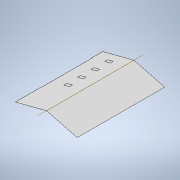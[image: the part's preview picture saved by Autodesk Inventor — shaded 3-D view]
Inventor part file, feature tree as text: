
AUTODESK INVENTOR PART (.ipt)
format: ipt  version: 2022.1 (Build 261234000, 234)  size: 143,872 bytes
history: native  units: in
note: dims shown in document units (in); Inventor stores cm internally (conversion verified against a paired STEP export)
features: other x2, sketch x2, extrude x2
ambient origin geometry x8: Origin, YZ Plane, XZ Plane, XY Plane, X Axis, Y Axis, Z Axis, Center Point
bodies: Body1 (feature_tree)
feature tree (6):
  other  "southPlaneOfRoof"
  other  "norhtPlaneOfRoof"
  sketch  "Sketch3"  dims[d7=0.0992in d8=-0.0992in]
  sketch  "Sketch4"  dims[d9=768.0in d10=279.0in d11=278.0in d12=279.0in d13=768.0in d14=279.0in d15=26.0in d16=51.0in d17=71.0in d18=94.0in d19=93.5in d20=94.0in d21=114.5in d22=114.0in d23=113.0in d24=114.0in d25=1.0in d26=0.0in d27=1.0in d28=0.0in d29=4.0in d30=216.0in d31=4.0in d32=104.0in]
  extrude  "Extrusion2"  [1 undecoded]
  extrude  "Extrusion3"  Depth=104.0in
note: 1 required parameter value undecoded (feature->parameter linkage not recoverable at this tier; creation-order binding heuristic only, values carry confidence <= 0.55)
